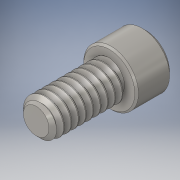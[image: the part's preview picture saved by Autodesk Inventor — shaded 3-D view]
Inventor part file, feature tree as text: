
AUTODESK INVENTOR PART (.ipt)
format: ipt  version: 2016 (Build 200138000, 138)  size: 550,400 bytes
history: native  units: in
note: dims shown in document units (in); Inventor stores cm internally (conversion verified against a paired STEP export)
features: chamfer x1
ambient origin geometry x8: Origin, YZ Plane, XZ Plane, XY Plane, X Axis, Y Axis, Z Axis, Center Point
bodies: Solid1 (feature_tree)
feature tree (1):
  chamfer  "Chamfer2"  [1 undecoded]
note: 1 required parameter value undecoded (feature->parameter linkage not recoverable at this tier; creation-order binding heuristic only, values carry confidence <= 0.55)
